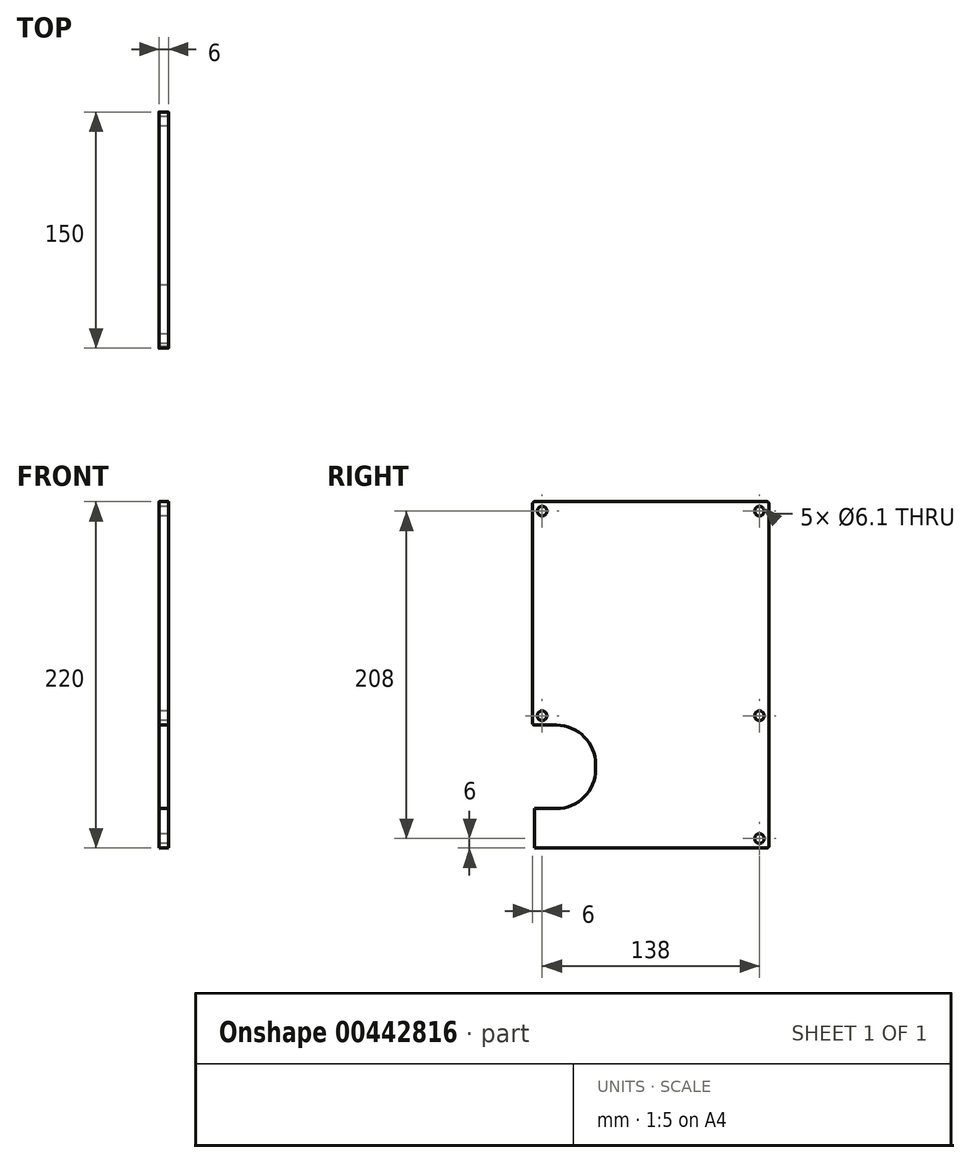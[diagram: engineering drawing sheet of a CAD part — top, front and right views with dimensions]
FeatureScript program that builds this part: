
annotation { "Feature Type Name" : "Feature", "Feature Type Description" : "" }
export const myFeature = defineFeature(function(context is Context, id is Id, definition is map)
    precondition{}
    {
        {
            var Q0;
            Q0=qCreatedBy(makeId("Right.planeOp"),FACE);
            var sketch = newSketch(context, id + "F0", { "sketchPlane" : qUnion([Q0])});
            skLineSegment(sketch, "E0.bottom", {"start": v(-1.27, 0) * mm, "end": v(-68.73, 0) * mm});
            skLineSegment(sketch, "E0.top", {"start": v(-1.27, 220) * mm, "end": v(-148.73, 220) * mm});
            skLineSegment(sketch, "E0.left", {"start": v(0, 1.27) * mm, "end": v(0, 218.73) * mm});
            skLineSegment(sketch, "E1.bottom", {"start": v(-148.93, 78) * mm, "end": v(-135, 78) * mm});
            skPoint(sketch, "E2.visualSharp", {"position": v(-70, 78) * mm});
            skLineSegment(sketch, "E3.trimOffspring", {"start": v(-150, 79.07) * mm, "end": v(-150, 218.73) * mm});
            skCircle(sketch, "E4", {"center": v(-144, 214) * mm, "radius": 3.05 * mm});
            skCircle(sketch, "E5", {"center": v(-6, 214) * mm, "radius": 3.05 * mm});
            skCircle(sketch, "E6", {"center": v(-6, 6) * mm, "radius": 3.05 * mm});
            skCircle(sketch, "E7", {"center": v(-144, 84) * mm, "radius": 3.05 * mm});
            skCircle(sketch, "E8", {"center": v(-6, 84) * mm, "radius": 3.05 * mm});
            skPoint(sketch, "E9.visualSharp", {"position": v(-150, 220) * mm});
            skArc(sketch, "E9.filletArc", {"start": v(-148.73, 220) * mm, "mid": v(-149.63, 219.63) * mm, "end": v(-150, 218.73) * mm});
            skPoint(sketch, "E10.visualSharp", {"position": v(0, 220) * mm});
            skArc(sketch, "E10.filletArc", {"start": v(0, 218.73) * mm, "mid": v(-0.37, 219.63) * mm, "end": v(-1.27, 220) * mm});
            skPoint(sketch, "E11.visualSharp", {"position": v(0, 0) * mm});
            skArc(sketch, "E11.filletArc", {"start": v(-1.27, 0) * mm, "mid": v(-0.37, 0.37) * mm, "end": v(0, 1.27) * mm});
            skPoint(sketch, "E12.visualSharp", {"position": v(-70, 0) * mm});
            skArc(sketch, "E12.filletArc", {"start": v(-70, 1.27) * mm, "mid": v(-69.63, 0.37) * mm, "end": v(-68.73, 0) * mm});
            skPoint(sketch, "E13.visualSharp", {"position": v(-150, 78) * mm});
            skArc(sketch, "E13.filletArc", {"start": v(-150, 79.07) * mm, "mid": v(-149.69, 78.31) * mm, "end": v(-148.93, 78) * mm});
            skLineSegment(sketch, "E14", {"start": v(-53.23, 0) * mm, "end": v(-148.93, 0) * mm});
            skLineSegment(sketch, "E15", {"start": v(-148.93, 0) * mm, "end": v(-148.93, 25) * mm});
            skLineSegment(sketch, "E16", {"start": v(-148.93, 25) * mm, "end": v(-135, 25) * mm});
            skLineSegment(sketch, "E17", {"start": v(-110, 53) * mm, "end": v(-110, 50) * mm});
            skPoint(sketch, "E18.visualSharp", {"position": v(-110, 78) * mm});
            skArc(sketch, "E18.filletArc", {"start": v(-110, 53) * mm, "mid": v(-117.32, 70.68) * mm, "end": v(-135, 78) * mm});
            skPoint(sketch, "E19.visualSharp", {"position": v(-110, 25) * mm});
            skArc(sketch, "E19.filletArc", {"start": v(-135, 25) * mm, "mid": v(-117.32, 32.32) * mm, "end": v(-110, 50) * mm});
            skSolve(sketch);
        }
        {
            var Q0;
            Q0 = qSketchRegion(id + "F0", true);
            extrude(context, id + "F1", {"entities" : qUnion([Q0]), "depth" : 6 * mm, "offsetDistance" : 25 * mm});
        }
    });
